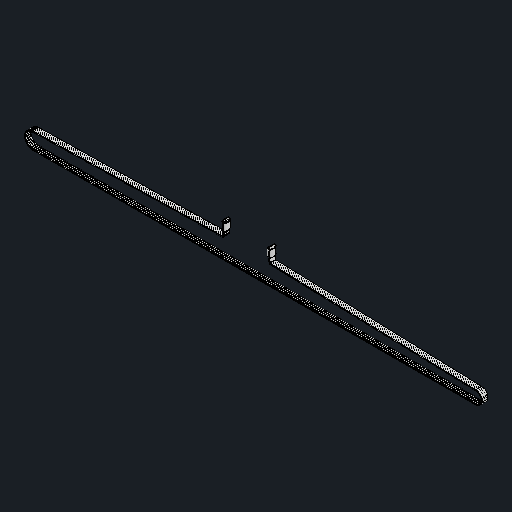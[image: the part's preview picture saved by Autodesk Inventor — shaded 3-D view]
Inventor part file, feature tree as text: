
AUTODESK INVENTOR PART (.ipt)
format: ipt  version: 2024.2 (Build 282272000, 272)  size: 1,966,080 bytes
history: native  units: mm
features: other x4, boolean_combine x1, mirror x1
ambient origin geometry x8: Origin, YZ Plane, XZ Plane, XY Plane, X Axis, Y Axis, Z Axis, Center Point
bodies: Body1 (feature_tree), Body2 (feature_tree), Body3 (feature_tree)
feature tree (6):
  other  "솔리드1"
  other  "솔리드2"
  other  "솔리드3"
  boolean_combine  "Combine1"
  mirror  "Mirror2"
  other  "Save Bodies1"
